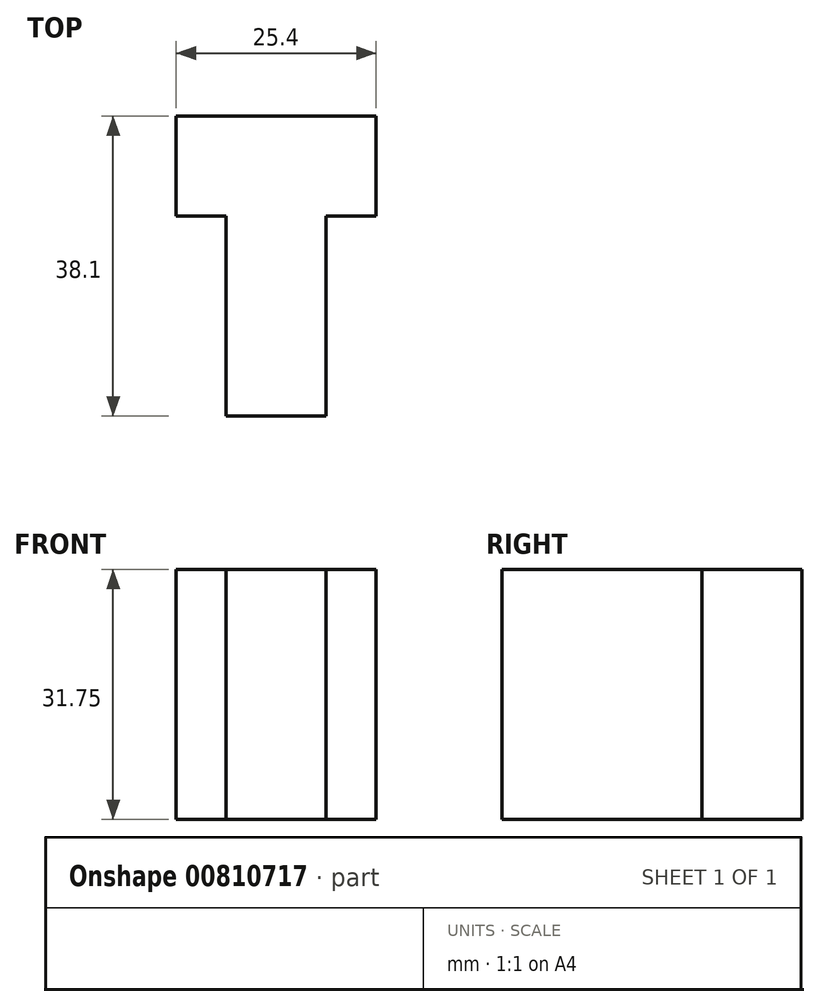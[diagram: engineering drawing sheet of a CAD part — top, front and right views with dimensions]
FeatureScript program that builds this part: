
annotation { "Feature Type Name" : "Feature", "Feature Type Description" : "" }
export const myFeature = defineFeature(function(context is Context, id is Id, definition is map)
    precondition{}
    {
        {
            var Q0;
            Q0=qCreatedBy(makeId("Top.planeOp"),FACE);
            var sketch = newSketch(context, id + "F0", { "sketchPlane" : qUnion([Q0])});
            skLineSegment(sketch, "E0.bottom", {"start": v(2.98, 4.45) * mm, "end": v(28.38, 4.45) * mm});
            skLineSegment(sketch, "E0.top", {"start": v(2.98, -33.65) * mm, "end": v(28.38, -33.65) * mm});
            skLineSegment(sketch, "E0.left", {"start": v(2.98, 4.45) * mm, "end": v(2.98, -33.65) * mm});
            skLineSegment(sketch, "E0.right", {"start": v(28.38, 4.45) * mm, "end": v(28.38, -33.65) * mm});
            skSolve(sketch);
        }
        {
            var Q0;
            Q0 = qSketchRegion(id + "F0", true);
            extrude(context, id + "F1", {"entities" : qUnion([Q0]), "depth" : 31.75 * mm, "offsetDistance" : 25.4 * mm});
        }
        {
            var Q0;
            Q0=makeQuery(id+"F1.opExtrude","CAP_FACE",FACE,{"disambiguationData":[OSD([sQuery(id+"F0.wireOp",EDGE,"E0.bottom"),sQuery(id+"F0.wireOp",EDGE,"E0.top"),sQuery(id+"F0.wireOp",EDGE,"E0.left"),sQuery(id+"F0.wireOp",EDGE,"E0.right")])],"isStart":false});
            var sketch = newSketch(context, id + "F2", { "sketchPlane" : qUnion([Q0])});
            skLineSegment(sketch, "E1.bottom", {"start": v(9.33, -33.65) * mm, "end": v(2.98, -33.65) * mm});
            skLineSegment(sketch, "E1.top", {"start": v(9.33, -8.25) * mm, "end": v(2.98, -8.25) * mm});
            skLineSegment(sketch, "E1.left", {"start": v(9.33, -33.65) * mm, "end": v(9.33, -8.25) * mm});
            skLineSegment(sketch, "E1.right", {"start": v(2.98, -33.65) * mm, "end": v(2.98, -8.25) * mm});
            skLineSegment(sketch, "E2.bottom", {"start": v(28.38, -33.65) * mm, "end": v(22.03, -33.65) * mm});
            skLineSegment(sketch, "E2.top", {"start": v(28.38, -8.25) * mm, "end": v(22.03, -8.25) * mm});
            skLineSegment(sketch, "E2.left", {"start": v(28.38, -33.65) * mm, "end": v(28.38, -8.25) * mm});
            skLineSegment(sketch, "E2.right", {"start": v(22.03, -33.65) * mm, "end": v(22.03, -8.25) * mm});
            skSolve(sketch);
        }
        {
            var Q0;
            Q0=makeQuery(id+"F2.imprint","IMPRINT",FACE,{"disambiguationData":[TD([[makeQuery(id+"F2.imprint","IMPRINT",EDGE,{"derivedFrom":sQuery(id+"F2.wireOp",EDGE,"E2.bottom")}),1.0]])]});
            extrude(context, id + "F3", {"entities" : qUnion([Q0]), "operationType" : NewBodyOperationType.REMOVE, "oppositeDirection" : true, "depth" : 31.75 * mm, "offsetDistance" : 25.4 * mm});
        }
        {
            var Q0;
            Q0=makeQuery(id+"F1.opExtrude","CAP_FACE",FACE,{"disambiguationData":[OSD([sQuery(id+"F0.wireOp",EDGE,"E0.bottom"),sQuery(id+"F0.wireOp",EDGE,"E0.top"),sQuery(id+"F0.wireOp",EDGE,"E0.left"),sQuery(id+"F0.wireOp",EDGE,"E0.right")])],"isStart":false});
            var sketch = newSketch(context, id + "F4", { "sketchPlane" : qUnion([Q0])});
            skLineSegment(sketch, "E3.bottom", {"start": v(2.98, -33.65) * mm, "end": v(9.33, -33.65) * mm});
            skLineSegment(sketch, "E3.top", {"start": v(2.98, -8.25) * mm, "end": v(9.33, -8.25) * mm});
            skLineSegment(sketch, "E3.left", {"start": v(2.98, -33.65) * mm, "end": v(2.98, -8.25) * mm});
            skLineSegment(sketch, "E3.right", {"start": v(9.33, -33.65) * mm, "end": v(9.33, -8.25) * mm});
            skSolve(sketch);
        }
        {
            var Q0;
            Q0 = qSketchRegion(id + "F4", true);
            extrude(context, id + "F5", {"entities" : qUnion([Q0]), "operationType" : NewBodyOperationType.REMOVE, "oppositeDirection" : true, "depth" : 31.75 * mm, "offsetDistance" : 25.4 * mm});
        }
    });
